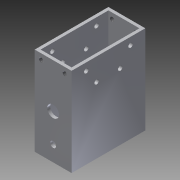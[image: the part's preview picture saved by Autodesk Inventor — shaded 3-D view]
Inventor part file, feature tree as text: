
AUTODESK INVENTOR PART (.ipt)
format: ipt  version: 2013 (Build 170138000, 138)  size: 182,784 bytes
history: native  units: mm
features: sketch x7, hole x5, thread x4, extrude x2, other x1
ambient origin geometry x1: Origin
feature tree (19):
  other  "ソリッド1"
  extrude  "押し出し1"  Depth=25.0mm
  extrude  "押し出し2"  Depth=50.0mm
  hole  "穴1"  [1 undecoded]
  hole  "穴2"  [1 undecoded]
  hole  "穴4"  [1 undecoded]
  thread  "ねじ1"
  thread  "ねじ2"
  thread  "ねじ3"
  thread  "ねじ4"
  hole  "穴5"  [1 undecoded]
  hole  "穴7"  [1 undecoded]
  sketch  "スケッチ1"
  sketch  "スケッチ2"
  sketch  "スケッチ3"
  sketch  "スケッチ4"
  sketch  "スケッチ5"
  sketch  "スケッチ7"
  sketch  "スケッチ8"
note: 5 required parameter values undecoded (feature->parameter linkage not recoverable at this tier; creation-order binding heuristic only, values carry confidence <= 0.55)
